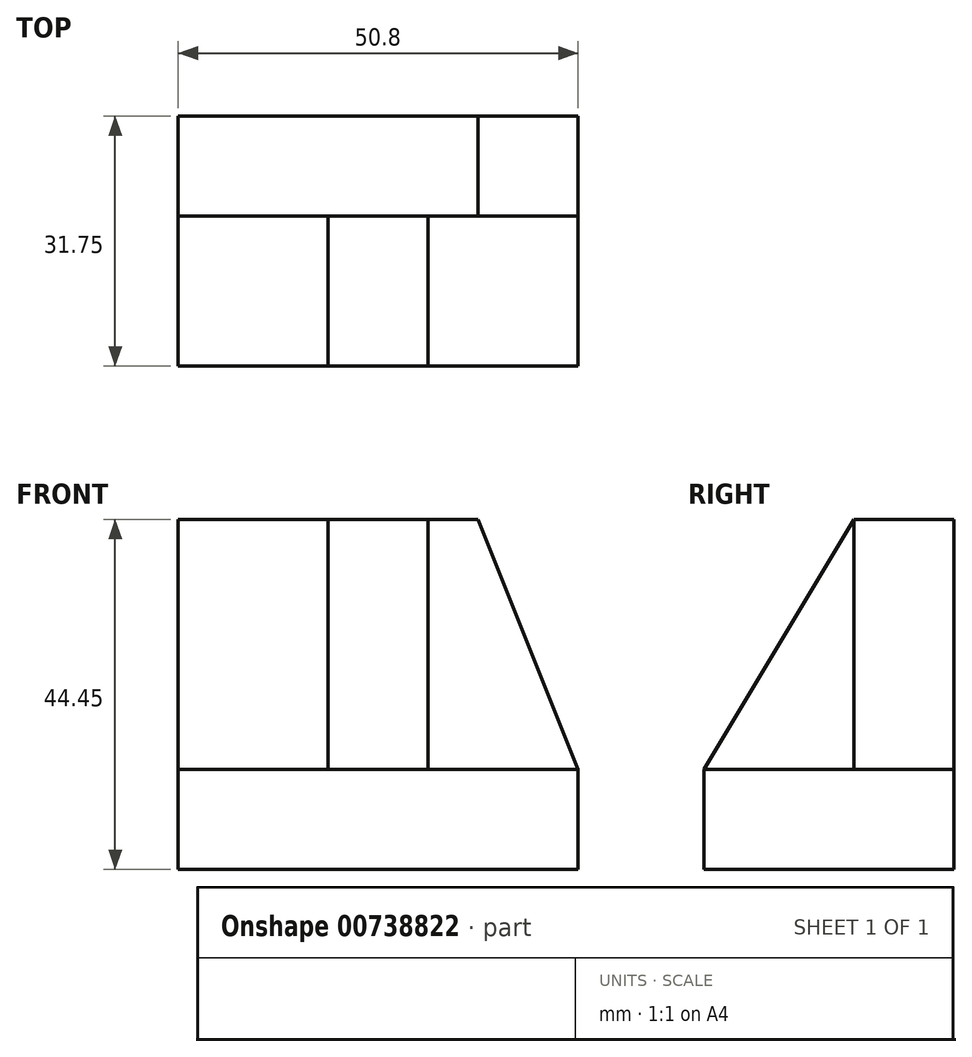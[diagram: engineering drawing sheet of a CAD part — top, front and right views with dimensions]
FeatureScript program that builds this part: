
annotation { "Feature Type Name" : "Feature", "Feature Type Description" : "" }
export const myFeature = defineFeature(function(context is Context, id is Id, definition is map)
    precondition{}
    {
        {
            var Q0;
            Q0=qCreatedBy(makeId("Front.planeOp"),FACE);
            var sketch = newSketch(context, id + "F0", { "sketchPlane" : qUnion([Q0])});
            skLineSegment(sketch, "E0", {"start": v(0, 0) * mm, "end": v(0, 31.75) * mm});
            skLineSegment(sketch, "E1", {"start": v(0, 31.75) * mm, "end": v(50.8, 31.75) * mm});
            skLineSegment(sketch, "E2", {"start": v(50.8, 31.75) * mm, "end": v(50.8, 0) * mm});
            skLineSegment(sketch, "E3", {"start": v(50.8, 0) * mm, "end": v(0, 0) * mm});
            skSolve(sketch);
        }
        {
            var Q0;
            Q0 = qSketchRegion(id + "F0", true);
            extrude(context, id + "F1", {"entities" : qUnion([Q0]), "depth" : 31.75 * mm, "offsetDistance" : 25.4 * mm});
        }
        {
            var Q0;
            Q0=makeQuery(id+"F1.opExtrude","CAP_FACE",FACE,{"disambiguationData":[OSD([sQuery(id+"F0.wireOp",EDGE,"E0"),sQuery(id+"F0.wireOp",EDGE,"E1"),sQuery(id+"F0.wireOp",EDGE,"E2"),sQuery(id+"F0.wireOp",EDGE,"E3")])],"isStart":false});
            var sketch = newSketch(context, id + "F2", { "sketchPlane" : qUnion([Q0])});
            skLineSegment(sketch, "E4", {"start": v(31.75, 31.75) * mm, "end": v(31.75, 0) * mm});
            skSolve(sketch);
        }
        {
            var Q0;
            {var subQ0=sQuery(id+"F2.wireOp",EDGE,"E4");Q0=makeQuery(id+"F2.imprint","IMPRINT",FACE,{"disambiguationData":[TD([[makeQuery(id+"F2.imprint","IMPRINT",EDGE,{"derivedFrom":subQ0}),1.0]])]});}
            extrude(context, id + "F3", {"entities" : qUnion([Q0]), "operationType" : NewBodyOperationType.REMOVE, "oppositeDirection" : true, "depth" : 19.05 * mm, "offsetDistance" : 25.4 * mm});
        }
        {
            var Q0;
            Q0=makeQuery(id+"F3.boolean.opBoolean","COPY",FACE,{"derivedFrom":makeQuery(id+"F3.opExtrude","CAP_FACE",FACE,{"disambiguationData":[OSD([sQuery(id+"F0.wireOp",EDGE,"E1"),sQuery(id+"F0.wireOp",EDGE,"E2"),sQuery(id+"F0.wireOp",EDGE,"E3"),sQuery(id+"F2.wireOp",EDGE,"E4")])],"isStart":false})});
            var sketch = newSketch(context, id + "F4", { "sketchPlane" : qUnion([Q0])});
            skLineSegment(sketch, "E5", {"start": v(38.1, 31.75) * mm, "end": v(50.8, 0) * mm});
            skSolve(sketch);
        }
        {
            var Q0;
            {var subQ0=sQuery(id+"F4.wireOp",EDGE,"E5");Q0=makeQuery(id+"F4.imprint","IMPRINT",FACE,{"disambiguationData":[TD([[makeQuery(id+"F4.imprint","IMPRINT",EDGE,{"derivedFrom":subQ0}),1.0]])]});}
            extrude(context, id + "F5", {"entities" : qUnion([Q0]), "operationType" : NewBodyOperationType.REMOVE, "endBound" : BoundingType.THROUGH_ALL, "oppositeDirection" : true, "depth" : 25.4 * mm, "offsetDistance" : 25.4 * mm});
        }
        {
            var Q0;
            Q0=makeQuery(id+"F3.boolean.opBoolean","COPY",FACE,{"derivedFrom":makeQuery(id+"F3.opExtrude","SWEPT_FACE",FACE,{"disambiguationData":[OSD([sQuery(id+"F2.wireOp",EDGE,"E4")])]})});
            var sketch = newSketch(context, id + "F6", { "sketchPlane" : qUnion([Q0])});
            skLineSegment(sketch, "E6", {"start": v(-12.7, 31.75) * mm, "end": v(-31.75, 0) * mm});
            skSolve(sketch);
        }
        {
            var Q0;
            Q0=makeQuery(id+"F6.imprint","IMPRINT",FACE,{"disambiguationData":[TD([[makeQuery(id+"F6.imprint","IMPRINT",EDGE,{"derivedFrom":sQuery(id+"F6.wireOp",EDGE,"E6")}),-1.0]])]});
            extrude(context, id + "F7", {"entities" : qUnion([Q0]), "operationType" : NewBodyOperationType.REMOVE, "oppositeDirection" : true, "depth" : 19.05 * mm, "offsetDistance" : 25.4 * mm});
        }
        {
            var Q0;
            Q0=makeQuery(id+"F1.opExtrude","SWEPT_FACE",FACE,{"disambiguationData":[OSD([sQuery(id+"F0.wireOp",EDGE,"E0")])]});
            var sketch = newSketch(context, id + "F8", { "sketchPlane" : qUnion([Q0])});
            skLineSegment(sketch, "E7", {"start": v(12.7, 31.75) * mm, "end": v(12.7, 0) * mm});
            skSolve(sketch);
        }
        {
            var Q0;
            {var subQ0=sQuery(id+"F8.wireOp",EDGE,"E7");Q0=makeQuery(id+"F8.imprint","IMPRINT",FACE,{"disambiguationData":[TD([[makeQuery(id+"F8.imprint","IMPRINT",EDGE,{"derivedFrom":subQ0}),1.0]])]});}
            extrude(context, id + "F9", {"entities" : qUnion([Q0]), "operationType" : NewBodyOperationType.REMOVE, "oppositeDirection" : true, "depth" : 19.05 * mm, "offsetDistance" : 25.4 * mm});
        }
        {
            var Q0;
            Q0=makeQuery(id+"F1.opExtrude","SWEPT_FACE",FACE,{"disambiguationData":[OSD([sQuery(id+"F0.wireOp",EDGE,"E3")])]});
            var sketch = newSketch(context, id + "F10", { "sketchPlane" : qUnion([Q0])});
            skLineSegment(sketch, "E8", {"start": v(0, 0) * mm, "end": v(0, 31.75) * mm});
            skLineSegment(sketch, "E9", {"start": v(0, 31.75) * mm, "end": v(50.8, 31.75) * mm});
            skLineSegment(sketch, "E10", {"start": v(50.8, 0) * mm, "end": v(50.8, 31.75) * mm});
            skLineSegment(sketch, "E11", {"start": v(50.8, 0) * mm, "end": v(0, 0) * mm});
            skSolve(sketch);
        }
        {
            var Q0;
            Q0 = qSketchRegion(id + "F10", true);
            extrude(context, id + "F11", {"entities" : qUnion([Q0]), "depth" : 12.7 * mm, "offsetDistance" : 25.4 * mm});
        }
    });
